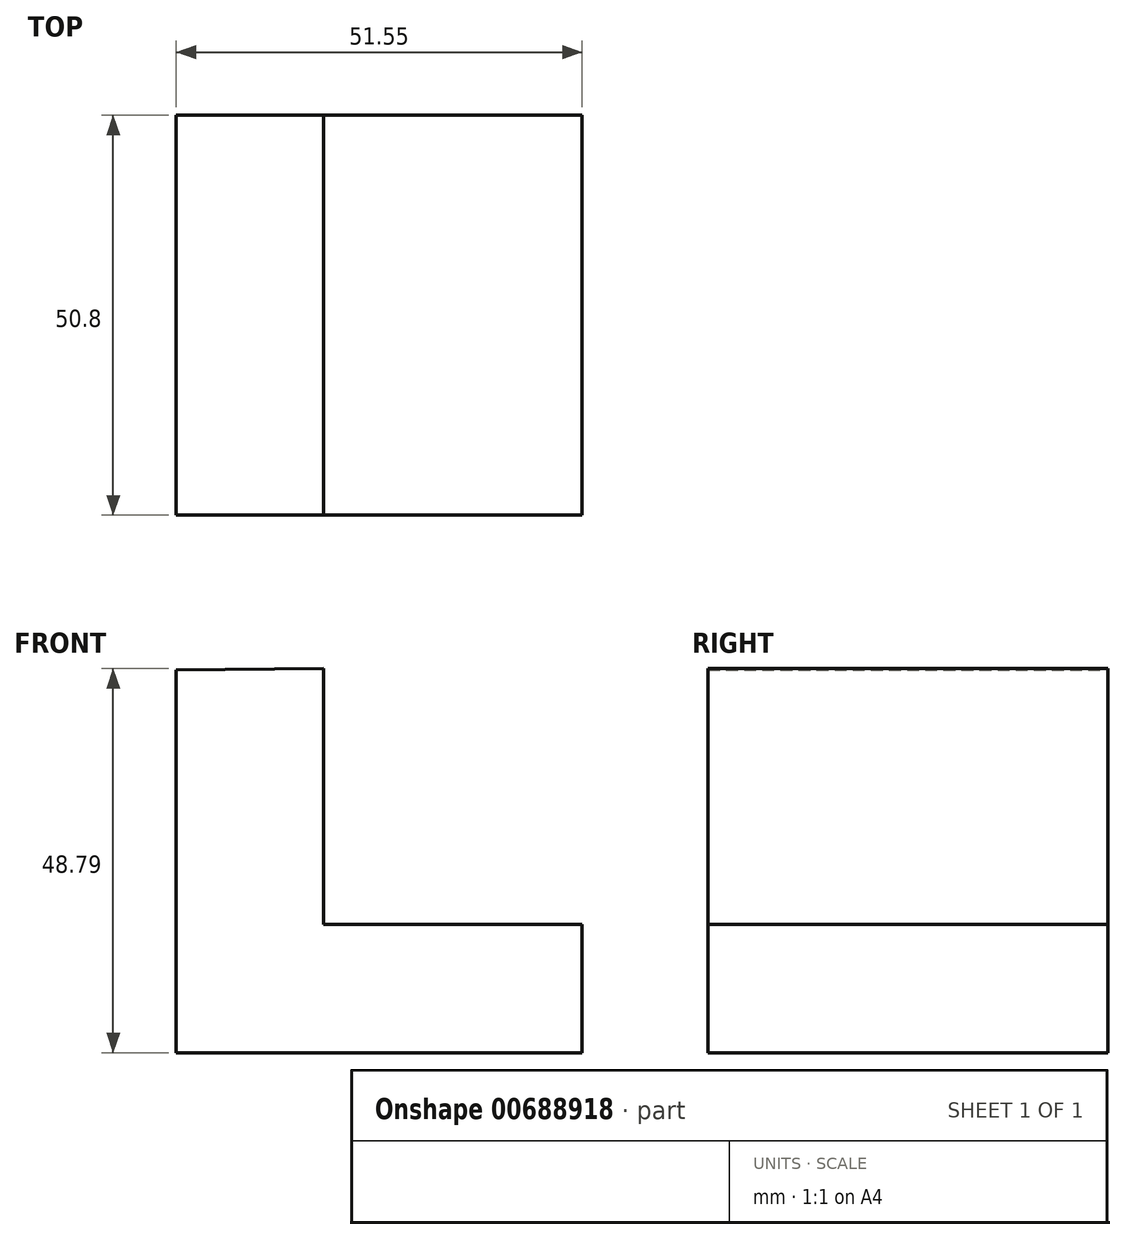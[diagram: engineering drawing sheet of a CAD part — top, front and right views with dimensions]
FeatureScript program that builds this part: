
annotation { "Feature Type Name" : "Feature", "Feature Type Description" : "" }
export const myFeature = defineFeature(function(context is Context, id is Id, definition is map)
    precondition{}
    {
        {
            var Q0;
            Q0=qCreatedBy(makeId("Front.planeOp"),FACE);
            var sketch = newSketch(context, id + "F0", { "sketchPlane" : qUnion([Q0])});
            skLineSegment(sketch, "E0", {"start": v(-29.7, 48.6) * mm, "end": v(-29.7, 0) * mm});
            skLineSegment(sketch, "E1", {"start": v(-29.7, 0) * mm, "end": v(21.86, 0) * mm});
            skLineSegment(sketch, "E2", {"start": v(21.86, 0) * mm, "end": v(21.86, 16.33) * mm});
            skLineSegment(sketch, "E3", {"start": v(21.86, 16.33) * mm, "end": v(-10.98, 16.33) * mm});
            skLineSegment(sketch, "E4", {"start": v(-10.98, 16.33) * mm, "end": v(-10.98, 48.79) * mm});
            skLineSegment(sketch, "E5", {"start": v(-10.98, 48.79) * mm, "end": v(-29.7, 48.6) * mm});
            skSolve(sketch);
        }
        {
            var Q0;
            Q0 = qSketchRegion(id + "F0", true);
            extrude(context, id + "F1", {"entities" : qUnion([Q0]), "depth" : 50.8 * mm, "offsetDistance" : 25.4 * mm});
        }
    });
